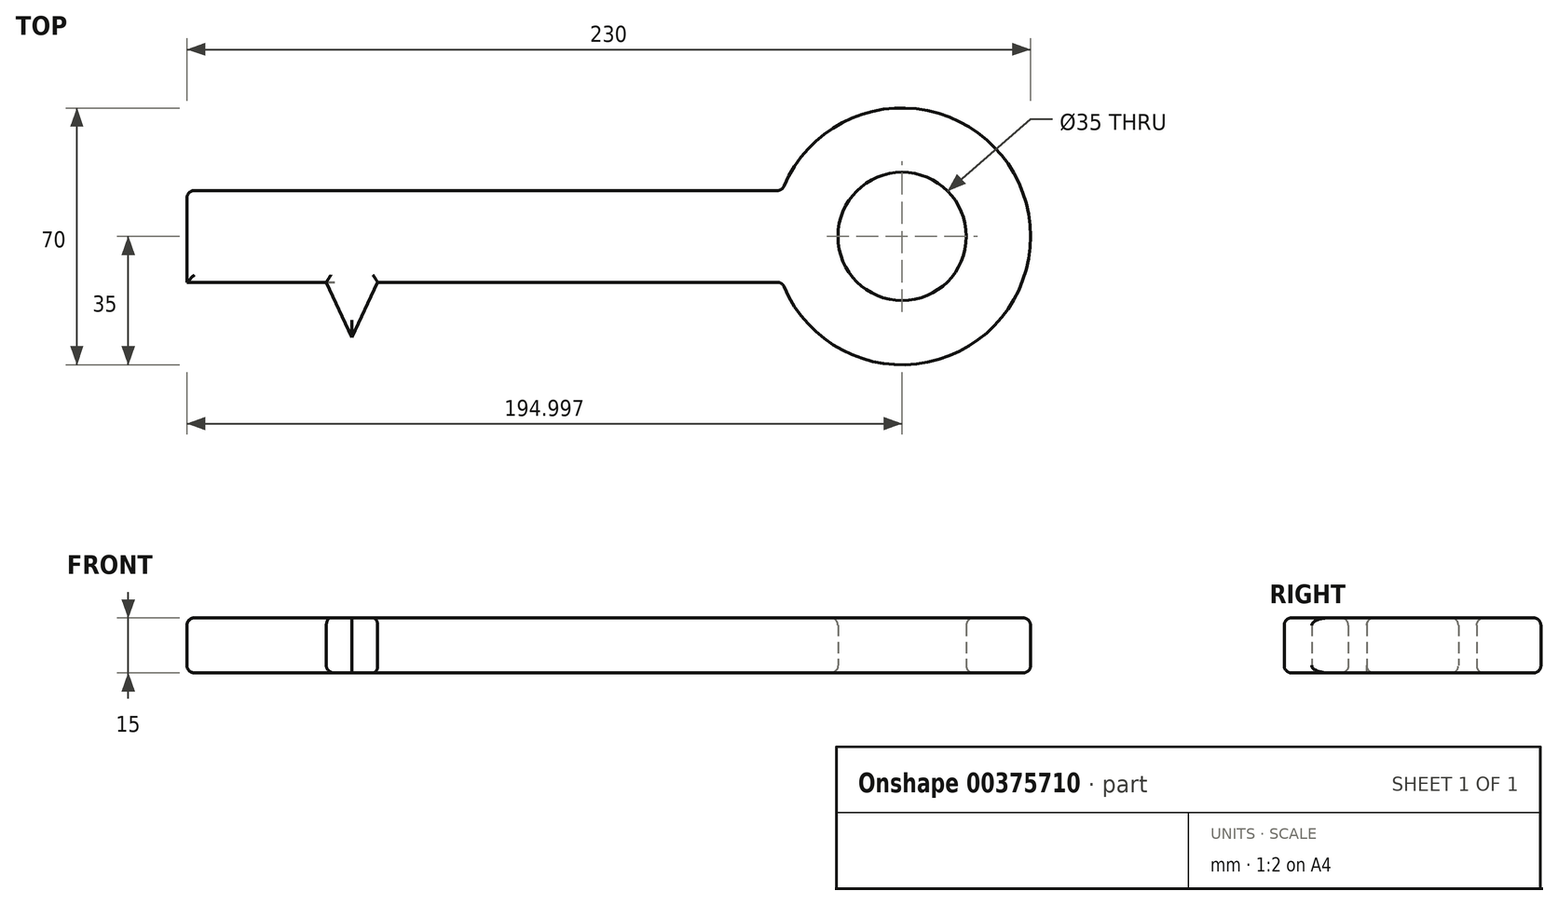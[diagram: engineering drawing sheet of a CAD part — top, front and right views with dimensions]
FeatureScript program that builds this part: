
annotation { "Feature Type Name" : "Feature", "Feature Type Description" : "" }
export const myFeature = defineFeature(function(context is Context, id is Id, definition is map)
    precondition{}
    {
        {
            var Q0;
            Q0=qCreatedBy(makeId("Top.planeOp"),FACE);
            var sketch = newSketch(context, id + "F0", { "sketchPlane" : qUnion([Q0])});
            skLineSegment(sketch, "E0.bottom", {"start": v(-87.25, 25) * mm, "end": v(75.06, 25) * mm});
            skLineSegment(sketch, "E0.top", {"start": v(-87.25, 0) * mm, "end": v(75.06, 0) * mm});
            skLineSegment(sketch, "E0.left", {"start": v(-87.25, 25) * mm, "end": v(-87.25, 0) * mm});
            skLineSegment(sketch, "E1.bottom", {"start": v(-87.25, 0) * mm, "end": v(-77.25, 0) * mm});
            skLineSegment(sketch, "E1.top", {"start": v(-87.25, -30) * mm, "end": v(-77.25, -30) * mm});
            skLineSegment(sketch, "E1.left", {"start": v(-87.25, 0) * mm, "end": v(-87.25, -30) * mm});
            skLineSegment(sketch, "E1.right", {"start": v(-77.25, 0) * mm, "end": v(-77.25, -30) * mm});
            skLineSegment(sketch, "E2.bottom", {"start": v(-67.25, 0) * mm, "end": v(-59.25, 0) * mm});
            skLineSegment(sketch, "E2.top", {"start": v(-67.25, -15) * mm, "end": v(-59.25, -15) * mm});
            skLineSegment(sketch, "E2.left", {"start": v(-67.25, 0) * mm, "end": v(-67.25, -15) * mm});
            skLineSegment(sketch, "E2.right", {"start": v(-59.25, 0) * mm, "end": v(-59.25, -15) * mm});
            skLineSegment(sketch, "E3", {"start": v(-49.25, 0) * mm, "end": v(-42.24, -15) * mm});
            skLineSegment(sketch, "E4", {"start": v(-42.24, -15) * mm, "end": v(-35.24, 0) * mm});
            skArc(sketch, "E5", {"start": v(75.06, 0) * mm, "mid": v(142.75, 12.5) * mm, "end": v(75.06, 25) * mm});
            skCircle(sketch, "E6", {"center": v(107.75, 12.5) * mm, "radius": 17.5 * mm});
            skLineSegment(sketch, "E7", {"start": v(107.75, 12.5) * mm, "end": v(-87.25, 12.5) * mm, "construction": true});
            skSolve(sketch);
        }
        {
            var Q0;
            Q0=makeQuery(id+"F0.imprint","IMPRINT",FACE,{"disambiguationData":[TD([[makeQuery(id+"F0.imprint","IMPRINT",EDGE,{"derivedFrom":sQuery(id+"F0.wireOp",EDGE,"E1.bottom")}),-1.0]])]});
            var Q1;
            {var subQ0=sQuery(id+"F0.wireOp",EDGE,"E3");Q1=makeQuery(id+"F0.imprint","IMPRINT",FACE,{"disambiguationData":[TD([[makeQuery(id+"F0.imprint","IMPRINT",EDGE,{"derivedFrom":subQ0}),1.0]])]});}
            var Q2;
            Q2=makeQuery(id+"F0.imprint","IMPRINT",FACE,{"disambiguationData":[TD([[makeQuery(id+"F0.imprint","IMPRINT",EDGE,{"derivedFrom":sQuery(id+"F0.wireOp",EDGE,"E0.bottom")}),-1.0]])]});
            var Q3;
            Q3=makeQuery(id+"F0.imprint","IMPRINT",FACE,{"disambiguationData":[TD([[makeQuery(id+"F0.imprint","IMPRINT",EDGE,{"derivedFrom":sQuery(id+"F0.wireOp",EDGE,"E2.bottom")}),-1.0]])]});
            extrude(context, id + "F1", {"entities" : qUnion([Q0, Q1, Q2, Q3]), "depth" : 15 * mm});
        }
        {
            var Q0;
            Q0=makeQuery(id+"F1.opExtrude","CAP_FACE",FACE,{"disambiguationData":[OSD([sQuery(id+"F0.wireOp",EDGE,"E0.bottom"),sQuery(id+"F0.wireOp",EDGE,"E0.top"),sQuery(id+"F0.wireOp",EDGE,"E0.left"),sQuery(id+"F0.wireOp",EDGE,"E1.top"),sQuery(id+"F0.wireOp",EDGE,"E1.left"),sQuery(id+"F0.wireOp",EDGE,"E1.right"),sQuery(id+"F0.wireOp",EDGE,"E2.top"),sQuery(id+"F0.wireOp",EDGE,"E2.left"),sQuery(id+"F0.wireOp",EDGE,"E2.right"),sQuery(id+"F0.wireOp",EDGE,"E3"),sQuery(id+"F0.wireOp",EDGE,"E4"),sQuery(id+"F0.wireOp",EDGE,"E5"),sQuery(id+"F0.wireOp",EDGE,"E6")])],"isStart":false});
            var Q1;
            Q1=makeQuery(id+"F1.opExtrude","CAP_EDGE",EDGE,{"disambiguationData":[OSD([sQuery(id+"F0.wireOp",EDGE,"E2.right")])],"isStart":false});
            var Q2;
            {var subQ0=sQuery(id+"F0.wireOp",EDGE,"E0.top");Q2=makeQuery(id+"F1.opExtrude","CAP_EDGE",EDGE,{"disambiguationData":[OSD([subQ0]),TDD([makeQuery(id+"F0.imprint","IMPRINT",EDGE,{"disambiguationData":[TD([[makeQuery(id+"F0.imprint","INTERSECT",VERTEX,{"derivedFrom":[subQ0,sQuery(id+"F0.wireOp",EDGE,"E5")]}),1.0]])],"derivedFrom":subQ0})])],"isStart":true});}
            var Q3;
            Q3=makeQuery(id+"F1.opExtrude","SWEPT_FACE",FACE,{"disambiguationData":[OSD([sQuery(id+"F0.wireOp",EDGE,"E5")])]});
            var Q4;
            Q4=makeQuery(id+"F1.opExtrude","CAP_EDGE",EDGE,{"disambiguationData":[OSD([sQuery(id+"F0.wireOp",EDGE,"E4")])],"isStart":true});
            var Q5;
            Q5=makeQuery(id+"F1.opExtrude","CAP_EDGE",EDGE,{"disambiguationData":[OSD([sQuery(id+"F0.wireOp",EDGE,"E3")])],"isStart":true});
            var Q6;
            Q6=makeQuery(id+"F1.opExtrude","CAP_EDGE",EDGE,{"disambiguationData":[OSD([sQuery(id+"F0.wireOp",EDGE,"E2.top")])],"isStart":true});
            var Q7;
            Q7=makeQuery(id+"F1.opExtrude","CAP_EDGE",EDGE,{"disambiguationData":[OSD([sQuery(id+"F0.wireOp",EDGE,"E1.top")])],"isStart":true});
            var Q8;
            Q8=makeQuery(id+"F1.opExtrude","SWEPT_FACE",FACE,{"disambiguationData":[OSD([sQuery(id+"F0.wireOp",EDGE,"E0.bottom")])]});
            var Q9;
            Q9=makeQuery(id+"F1.opExtrude","CAP_EDGE",EDGE,{"disambiguationData":[OSD([sQuery(id+"F0.wireOp",EDGE,"E2.left")])],"isStart":true});
            var Q10;
            Q10=makeQuery(id+"F1.opExtrude","CAP_EDGE",EDGE,{"disambiguationData":[OSD([sQuery(id+"F0.wireOp",EDGE,"E0.left"),sQuery(id+"F0.wireOp",EDGE,"E1.left")])],"isStart":true});
            var Q11;
            Q11=makeQuery(id+"F1.opExtrude","CAP_EDGE",EDGE,{"disambiguationData":[OSD([sQuery(id+"F0.wireOp",EDGE,"E6")])],"isStart":true});
            fillet(context, id + "F2", {"entities" : qUnion([Q0, Q1, Q2, Q3, Q4, Q5, Q6, Q7, Q8, Q9, Q10, Q11]), "radius" : 2 * mm, "tangentPropagation" : true, "allowEdgeOverflow" : false});
        }
    });
